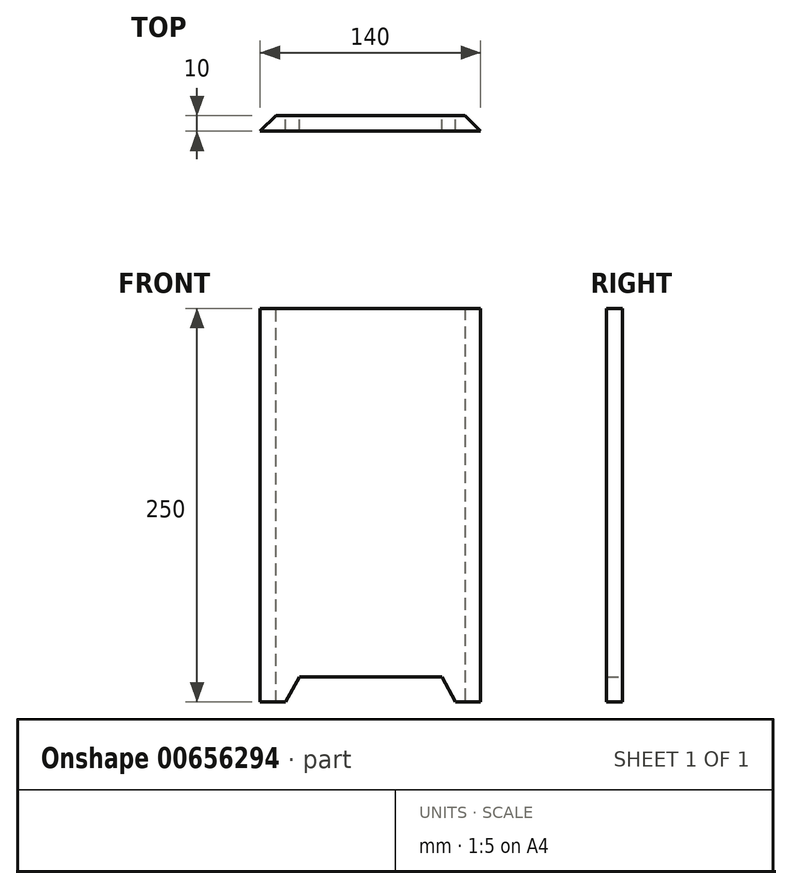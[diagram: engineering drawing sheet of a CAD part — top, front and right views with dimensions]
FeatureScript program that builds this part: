
annotation { "Feature Type Name" : "Feature", "Feature Type Description" : "" }
export const myFeature = defineFeature(function(context is Context, id is Id, definition is map)
    precondition{}
    {
        {
            var Q0;
            Q0=qCreatedBy(makeId("Front.planeOp"),FACE);
            var sketch = newSketch(context, id + "F0", { "sketchPlane" : qUnion([Q0])});
            skLineSegment(sketch, "E0.bottom", {"start": v(70, 125) * mm, "end": v(-70, 125) * mm});
            skLineSegment(sketch, "E0.top", {"start": v(70, -125) * mm, "end": v(54, -125) * mm});
            skLineSegment(sketch, "E0.left", {"start": v(70, 125) * mm, "end": v(70, -125) * mm});
            skLineSegment(sketch, "E0.right", {"start": v(-70, 125) * mm, "end": v(-70, -125) * mm});
            skPoint(sketch, "E0.middle", {"position": v(0, 0) * mm});
            skPoint(sketch, "E1.end.orphan", {"position": v(54, -125) * mm});
            skPoint(sketch, "E2.MirrorP", {"position": v(-89.87, -20.7) * mm});
            skLineSegment(sketch, "E3", {"start": v(-45, -109) * mm, "end": v(45.5, -109) * mm});
            skLineSegment(sketch, "E4", {"start": v(-54, -125) * mm, "end": v(-45, -109) * mm});
            skPoint(sketch, "E5.orphan", {"position": v(-70, -109) * mm});
            skLineSegment(sketch, "E6.trimOffspring", {"start": v(-54, -125) * mm, "end": v(-70, -125) * mm});
            skPoint(sketch, "E7.end.orphan", {"position": v(70, 80) * mm});
            skPoint(sketch, "E7.start.orphan", {"position": v(35, 125) * mm});
            skPoint(sketch, "E8.end.orphan", {"position": v(-35, 125) * mm});
            skPoint(sketch, "E8.start.orphan", {"position": v(-70, 80) * mm});
            skLineSegment(sketch, "E9", {"start": v(70.5, -108.86) * mm, "end": v(70, -108.86) * mm});
            skLineSegment(sketch, "E10", {"start": v(45.5, -109) * mm, "end": v(54, -125) * mm});
            skSolve(sketch);
        }
        {
            var Q0;
            {var subQ1=sQuery(id+"F0.wireOp",EDGE,"E0.bottom");Q0=makeQuery(id+"F0.imprint","IMPRINT",FACE,{"disambiguationData":[TD([[makeQuery(id+"F0.imprint","IMPRINT",EDGE,{"derivedFrom":subQ1}),1.0]])]});}
            var Q1;
            {var subQ0=sQuery(id+"F0.wireOp",EDGE,"E0.top");Q1=makeQuery(id+"F0.imprint","IMPRINT",FACE,{"disambiguationData":[TD([[makeQuery(id+"F0.imprint","IMPRINT",EDGE,{"derivedFrom":subQ0}),-1.0]])]});}
            extrude(context, id + "F1", {"entities" : qUnion([Q0, Q1]), "depth" : 10 * mm, "offsetDistance" : 25 * mm});
        }
        {
            var Q0;
            Q0=makeQuery(id+"F1.opExtrude","CAP_EDGE",EDGE,{"disambiguationData":[OSD([sQuery(id+"F0.wireOp",EDGE,"E0.right")])],"isStart":true});
            var Q1;
            Q1=makeQuery(id+"F1.opExtrude","CAP_EDGE",EDGE,{"disambiguationData":[OSD([sQuery(id+"F0.wireOp",EDGE,"E0.left")])],"isStart":true});
            chamfer(context, id + "F2", {"entities" : qUnion([Q0, Q1]), "width" : 10 * mm, "tangentPropagation" : true});
        }
    });
